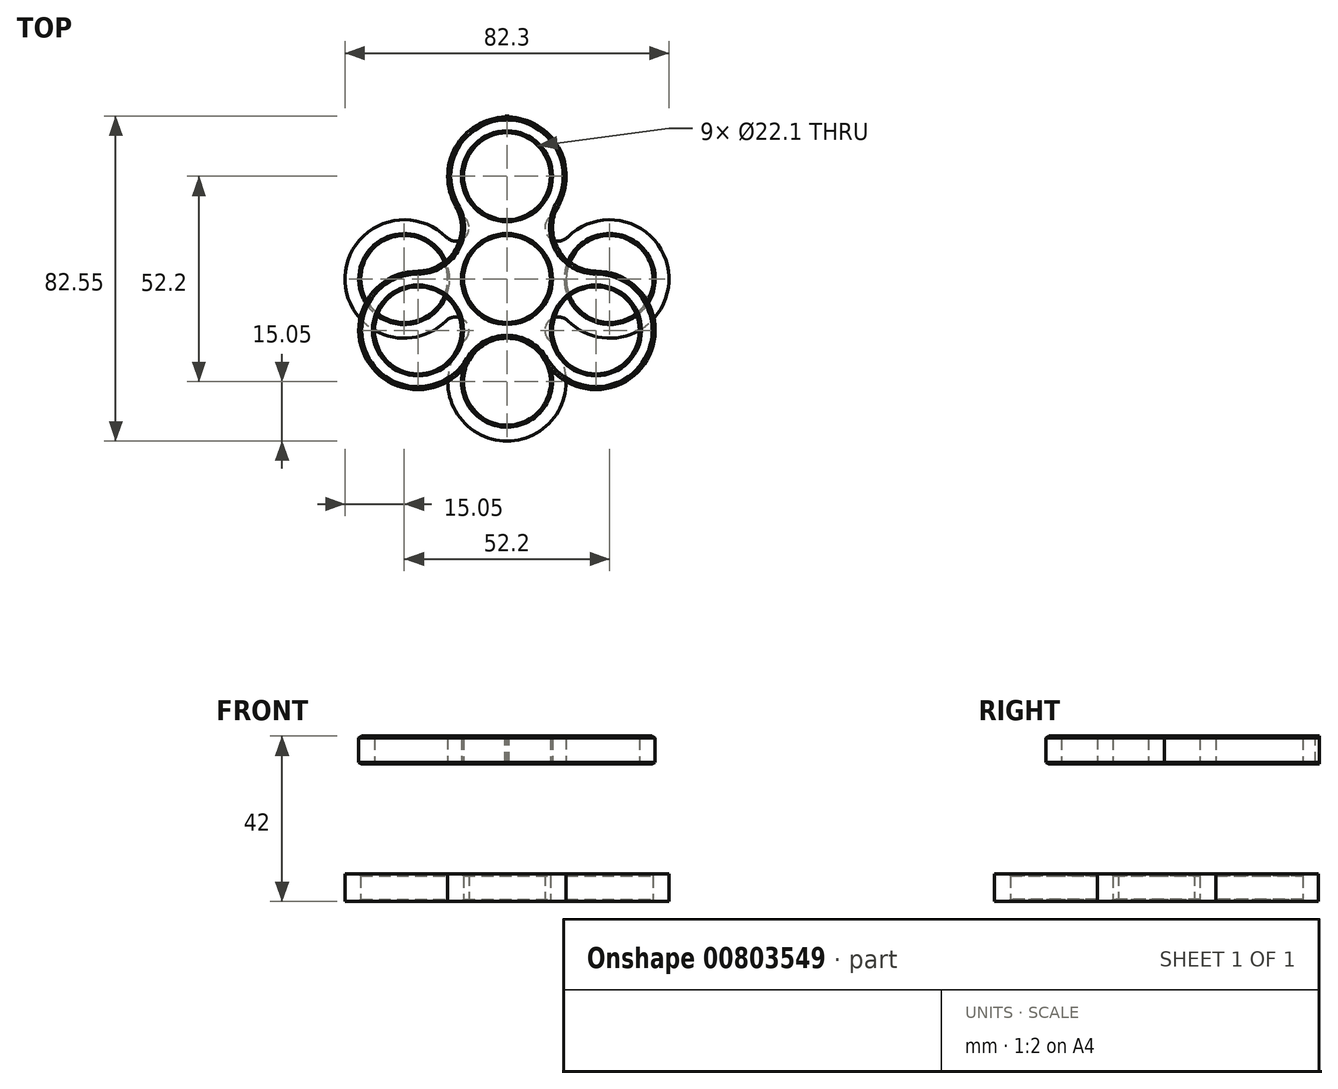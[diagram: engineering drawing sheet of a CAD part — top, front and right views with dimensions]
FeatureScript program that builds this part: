
annotation { "Feature Type Name" : "Feature", "Feature Type Description" : "" }
export const myFeature = defineFeature(function(context is Context, id is Id, definition is map)
    precondition{}
    {
        {
            var Q0;
            Q0=qCreatedBy(makeId("Top.planeOp"),FACE);
            var sketch = newSketch(context, id + "F0", { "sketchPlane" : qUnion([Q0])});
            skCircle(sketch, "E0", {"center": v(0, 0) * mm, "radius": 11.05 * mm});
            skCircle(sketch, "E1", {"center": v(0, 26.1) * mm, "radius": 11.05 * mm});
            skCircle(sketch, "E2", {"center": v(22.6, -13.05) * mm, "radius": 11.05 * mm});
            skCircle(sketch, "E3", {"center": v(-22.6, -13.05) * mm, "radius": 11.05 * mm});
            skLineSegment(sketch, "E4", {"start": v(0, 26.1) * mm, "end": v(-22.6, -13.05) * mm, "construction": true});
            skLineSegment(sketch, "E5", {"start": v(-22.6, -13.05) * mm, "end": v(22.6, -13.05) * mm, "construction": true});
            skLineSegment(sketch, "E6", {"start": v(22.6, -13.05) * mm, "end": v(0, 26.1) * mm, "construction": true});
            skLineSegment(sketch, "E7", {"start": v(11.3, 6.52) * mm, "end": v(-22.6, -13.05) * mm, "construction": true});
            skArc(sketch, "E8", {"start": v(13.03, 18.58) * mm, "mid": v(0, 41.15) * mm, "end": v(-13.03, 18.58) * mm});
            skLineSegment(sketch, "E9", {"start": v(-13.03, 7.52) * mm, "end": v(-13.03, 7.52) * mm});
            skArc(sketch, "E10", {"start": v(-22.6, 2) * mm, "mid": v(-35.64, -20.57) * mm, "end": v(-9.57, -20.58) * mm});
            skArc(sketch, "E11", {"start": v(9.57, -20.57) * mm, "mid": v(35.64, -20.57) * mm, "end": v(22.6, 2) * mm});
            skLineSegment(sketch, "E12.trimOffspring", {"start": v(13.03, 7.52) * mm, "end": v(13.03, 7.52) * mm});
            skLineSegment(sketch, "E13.trimOffspring", {"start": v(0, -15.05) * mm, "end": v(0, -15.05) * mm});
            skPoint(sketch, "E14.visualSharp", {"position": v(7.5, 13.05) * mm});
            skArc(sketch, "E14.filletArc", {"start": v(13.03, 18.58) * mm, "mid": v(11.55, 13.05) * mm, "end": v(13.03, 7.52) * mm});
            skPoint(sketch, "E15.visualSharp", {"position": v(15.05, -0.03) * mm});
            skArc(sketch, "E15.filletArc", {"start": v(13.03, 7.52) * mm, "mid": v(17.08, 3.48) * mm, "end": v(22.6, 2) * mm});
            skPoint(sketch, "E16.visualSharp", {"position": v(7.55, -13.02) * mm});
            skArc(sketch, "E16.filletArc", {"start": v(9.57, -20.57) * mm, "mid": v(5.52, -16.53) * mm, "end": v(0, -15.05) * mm});
            skPoint(sketch, "E17.visualSharp", {"position": v(-7.55, -13.02) * mm});
            skArc(sketch, "E17.filletArc", {"start": v(0, -15.05) * mm, "mid": v(-5.53, -16.53) * mm, "end": v(-9.57, -20.57) * mm});
            skPoint(sketch, "E18.visualSharp", {"position": v(-15.05, -0.03) * mm});
            skArc(sketch, "E18.filletArc", {"start": v(-22.6, 2) * mm, "mid": v(-17.08, 3.48) * mm, "end": v(-13.03, 7.52) * mm});
            skPoint(sketch, "E19.visualSharp", {"position": v(-7.5, 13.05) * mm});
            skArc(sketch, "E19.filletArc", {"start": v(-13.03, 7.52) * mm, "mid": v(-11.55, 13.05) * mm, "end": v(-13.03, 18.58) * mm});
            skCircle(sketch, "E20", {"center": v(0, 0) * mm, "radius": 41.15 * mm, "construction": true});
            skSolve(sketch);
        }
        {
            var Q0;
            Q0=makeQuery(id+"F0.imprint","IMPRINT",FACE,{"disambiguationData":[TD([[makeQuery(id+"F0.imprint","IMPRINT",EDGE,{"derivedFrom":sQuery(id+"F0.wireOp",EDGE,"E0")}),-1.0]])]});
            extrude(context, id + "F1", {"entities" : qUnion([Q0]), "depth" : 7 * mm, "offsetDistance" : 25 * mm});
        }
        {
            var Q0;
            Q0=makeQuery(id+"F1.opExtrude","SWEPT_FACE",FACE,{"disambiguationData":[OSD([sQuery(id+"F0.wireOp",EDGE,"E3")])]});
            var Q1;
            Q1=makeQuery(id+"F1.opExtrude","SWEPT_FACE",FACE,{"disambiguationData":[OSD([sQuery(id+"F0.wireOp",EDGE,"E0")])]});
            var Q2;
            Q2=makeQuery(id+"F1.opExtrude","SWEPT_FACE",FACE,{"disambiguationData":[OSD([sQuery(id+"F0.wireOp",EDGE,"E1")])]});
            var Q3;
            Q3=makeQuery(id+"F1.opExtrude","SWEPT_FACE",FACE,{"disambiguationData":[OSD([sQuery(id+"F0.wireOp",EDGE,"E2")])]});
            chamfer(context, id + "F2", {"entities" : qUnion([Q0, Q1, Q2, Q3]), "width" : .5 * mm, "tangentPropagation" : true});
        }
        {
            var Q0;
            Q0=makeQuery(id+"F2.opChamfer","SPLIT",FACE,{"disambiguationData":[OD(1.0)],"derivedFrom":makeQuery(id+"F1.opExtrude","CAP_FACE",FACE,{"disambiguationData":[OSD([sQuery(id+"F0.wireOp",EDGE,"E0"),sQuery(id+"F0.wireOp",EDGE,"E1"),sQuery(id+"F0.wireOp",EDGE,"E2"),sQuery(id+"F0.wireOp",EDGE,"E3"),sQuery(id+"F0.wireOp",EDGE,"E8"),sQuery(id+"F0.wireOp",EDGE,"E10"),sQuery(id+"F0.wireOp",EDGE,"E11"),sQuery(id+"F0.wireOp",EDGE,"E14.filletArc"),sQuery(id+"F0.wireOp",EDGE,"E15.filletArc"),sQuery(id+"F0.wireOp",EDGE,"E16.filletArc"),sQuery(id+"F0.wireOp",EDGE,"E17.filletArc"),sQuery(id+"F0.wireOp",EDGE,"E18.filletArc"),sQuery(id+"F0.wireOp",EDGE,"E19.filletArc")])],"isStart":true})});
            cPlane(context, id + "F3", {"entities" : qUnion([Q0]), "cplaneType" : CPlaneType.OFFSET, "offset" : 35 * mm, "width" : 150 * mm, "height" : 150 * mm});
        }
        {
            var Q0;
            Q0=qCreatedBy(id+"F3.planeOp",FACE);
            var sketch = newSketch(context, id + "F4", { "sketchPlane" : qUnion([Q0])});
            skCircle(sketch, "E21", {"center": v(0, 0) * mm, "radius": 11.05 * mm});
            skCircle(sketch, "E22", {"center": v(0, 26.1) * mm, "radius": 11.05 * mm});
            skCircle(sketch, "E23", {"center": v(26.1, 0) * mm, "radius": 11.05 * mm});
            skCircle(sketch, "E24", {"center": v(0, -26.1) * mm, "radius": 11.05 * mm});
            skCircle(sketch, "E25", {"center": v(-26.1, 0) * mm, "radius": 11.05 * mm});
            skLineSegment(sketch, "E26", {"start": v(0, 26.1) * mm, "end": v(0, 0) * mm, "construction": true});
            skLineSegment(sketch, "E27", {"start": v(26.1, 0) * mm, "end": v(0, 0) * mm, "construction": true});
            skLineSegment(sketch, "E28", {"start": v(0, -26.1) * mm, "end": v(0, 0) * mm, "construction": true});
            skLineSegment(sketch, "E29", {"start": v(-26.1, 0) * mm, "end": v(0, 0) * mm, "construction": true});
            skArc(sketch, "E30", {"start": v(10.64, 15.46) * mm, "mid": v(0, 41.15) * mm, "end": v(-10.64, 15.46) * mm});
            skArc(sketch, "E31", {"start": v(15.46, -10.64) * mm, "mid": v(41.15, 0) * mm, "end": v(15.46, 10.64) * mm});
            skArc(sketch, "E32", {"start": v(-7.5, 13.05) * mm, "mid": v(-10.64, 10.64) * mm, "end": v(-13.05, 7.5) * mm, "construction": true});
            skArc(sketch, "E33", {"start": v(-10.64, -15.46) * mm, "mid": v(0, -41.15) * mm, "end": v(10.64, -15.46) * mm});
            skArc(sketch, "E34", {"start": v(-15.46, 10.64) * mm, "mid": v(-41.15, 0) * mm, "end": v(-15.46, -10.64) * mm});
            skArc(sketch, "E35.trimOffspring", {"start": v(-13.05, -7.5) * mm, "mid": v(-10.64, -10.64) * mm, "end": v(-7.5, -13.05) * mm, "construction": true});
            skArc(sketch, "E36.trimOffspring", {"start": v(7.5, -13.05) * mm, "mid": v(10.64, -10.64) * mm, "end": v(13.05, -7.5) * mm, "construction": true});
            skArc(sketch, "E37.trimOffspring", {"start": v(13.05, 7.5) * mm, "mid": v(10.64, 10.64) * mm, "end": v(7.5, 13.05) * mm, "construction": true});
            skArc(sketch, "E38", {"start": v(10.64, 15.46) * mm, "mid": v(10.64, 10.64) * mm, "end": v(15.46, 10.64) * mm});
            skArc(sketch, "E39", {"start": v(15.46, -10.64) * mm, "mid": v(10.64, -10.64) * mm, "end": v(10.64, -15.46) * mm});
            skArc(sketch, "E40", {"start": v(-10.64, -15.46) * mm, "mid": v(-10.64, -10.64) * mm, "end": v(-15.46, -10.64) * mm});
            skArc(sketch, "E41", {"start": v(-15.46, 10.64) * mm, "mid": v(-10.64, 10.64) * mm, "end": v(-10.64, 15.46) * mm});
            skSolve(sketch);
        }
        {
            var Q0;
            Q0=makeQuery(id+"F4.imprint","IMPRINT",FACE,{"disambiguationData":[TD([[makeQuery(id+"F4.imprint","IMPRINT",EDGE,{"derivedFrom":sQuery(id+"F4.wireOp",EDGE,"E21")}),-1.0]])]});
            extrude(context, id + "F5", {"entities" : qUnion([Q0]), "oppositeDirection" : true, "depth" : 7 * mm, "offsetDistance" : 25 * mm});
        }
        {
            var Q0;
            Q0=makeQuery(id+"F5.opExtrude","SWEPT_FACE",FACE,{"disambiguationData":[OSD([sQuery(id+"F4.wireOp",EDGE,"E25")])]});
            var Q1;
            Q1=makeQuery(id+"F5.opExtrude","SWEPT_FACE",FACE,{"disambiguationData":[OSD([sQuery(id+"F4.wireOp",EDGE,"E21")])]});
            var Q2;
            Q2=makeQuery(id+"F5.opExtrude","SWEPT_FACE",FACE,{"disambiguationData":[OSD([sQuery(id+"F4.wireOp",EDGE,"E24")])]});
            var Q3;
            Q3=makeQuery(id+"F5.opExtrude","SWEPT_FACE",FACE,{"disambiguationData":[OSD([sQuery(id+"F4.wireOp",EDGE,"E23")])]});
            var Q4;
            Q4=makeQuery(id+"F5.opExtrude","SWEPT_FACE",FACE,{"disambiguationData":[OSD([sQuery(id+"F4.wireOp",EDGE,"E22")])]});
            chamfer(context, id + "F6", {"entities" : qUnion([Q0, Q1, Q2, Q3, Q4]), "width" : .5 * mm, "tangentPropagation" : true});
        }
        {
            var Q0;
            Q0=makeQuery(id+"F1.opExtrude","CAP_FACE",FACE,{"disambiguationData":[OSD([sQuery(id+"F0.wireOp",EDGE,"E0"),sQuery(id+"F0.wireOp",EDGE,"E1"),sQuery(id+"F0.wireOp",EDGE,"E2"),sQuery(id+"F0.wireOp",EDGE,"E3"),sQuery(id+"F0.wireOp",EDGE,"E8"),sQuery(id+"F0.wireOp",EDGE,"E10"),sQuery(id+"F0.wireOp",EDGE,"E11"),sQuery(id+"F0.wireOp",EDGE,"E14.filletArc"),sQuery(id+"F0.wireOp",EDGE,"E15.filletArc"),sQuery(id+"F0.wireOp",EDGE,"E16.filletArc"),sQuery(id+"F0.wireOp",EDGE,"E17.filletArc"),sQuery(id+"F0.wireOp",EDGE,"E18.filletArc"),sQuery(id+"F0.wireOp",EDGE,"E19.filletArc")])],"isStart":false});
            var sketch = newSketch(context, id + "F7", { "sketchPlane" : qUnion([Q0])});
            skLineSegment(sketch, "E42", {"start": v(0, 40.4) * mm, "end": v(0.52, 41.4) * mm});
            skPoint(sketch, "E42.startSnap0", {"position": v(0, 41.15) * mm});
            skLineSegment(sketch, "E43", {"start": v(0.52, 41.4) * mm, "end": v(-0.52, 41.4) * mm});
            skLineSegment(sketch, "E44", {"start": v(-0.52, 41.4) * mm, "end": v(0, 40.4) * mm});
            skPoint(sketch, "E45", {"position": v(-3.48, 40.74) * mm});
            skPoint(sketch, "E46", {"position": v(-6.76, 39.54) * mm});
            skLineSegment(sketch, "E47", {"start": v(0, 41.15) * mm, "end": v(-3.48, 40.74) * mm, "construction": true});
            skLineSegment(sketch, "E48", {"start": v(-3.48, 40.74) * mm, "end": v(-6.76, 39.54) * mm, "construction": true});
            skLineSegment(sketch, "E49", {"start": v(-6.76, 39.54) * mm, "end": v(-9.69, 37.62) * mm, "construction": true});
            skLineSegment(sketch, "E50", {"start": v(-9.69, 37.62) * mm, "end": v(-12.09, 35.07) * mm, "construction": true});
            skLineSegment(sketch, "E51", {"start": v(-12.09, 35.07) * mm, "end": v(-13.83, 32.04) * mm, "construction": true});
            skLineSegment(sketch, "E52", {"start": v(-13.83, 32.04) * mm, "end": v(-14.83, 28.68) * mm, "construction": true});
            skLineSegment(sketch, "E53", {"start": v(-14.83, 28.68) * mm, "end": v(-15.02, 25.19) * mm, "construction": true});
            skLineSegment(sketch, "E54", {"start": v(-15.02, 25.19) * mm, "end": v(-14.4, 21.74) * mm, "construction": true});
            skLineSegment(sketch, "E55", {"start": v(-14.4, 21.74) * mm, "end": v(-13, 18.53) * mm, "construction": true});
            skLineSegment(sketch, "E56", {"start": v(-13, 18.53) * mm, "end": v(-11.78, 15.26) * mm, "construction": true});
            skLineSegment(sketch, "E57", {"start": v(-11.78, 15.26) * mm, "end": v(-11.63, 11.76) * mm, "construction": true});
            skSolve(sketch);
        }
        {
            var Q0;
            {var subQ2=sQuery(id+"F0.wireOp",EDGE,"E8");Q0=makeQuery(id+"F9.boolean.opBoolean","SPLIT",EDGE,{"disambiguationData":[TD([makeQuery(id+"F9.opExtrude","SWEPT_FACE",FACE,{"disambiguationData":[OSD([sQuery(id+"F7.wireOp",EDGE,"E44")])]})])],"derivedFrom":makeQuery(id+"F1.opExtrude","CAP_EDGE",EDGE,{"disambiguationData":[OSD([subQ2])],"isStart":false})});}
            var Q1;
            {var subQ2=sQuery(id+"F0.wireOp",EDGE,"E8");Q1=makeQuery(id+"F9.boolean.opBoolean","SPLIT",EDGE,{"disambiguationData":[TD([makeQuery(id+"F9.opExtrude","SWEPT_FACE",FACE,{"disambiguationData":[OSD([sQuery(id+"F7.wireOp",EDGE,"E44")])]})])],"derivedFrom":makeQuery(id+"F1.opExtrude","CAP_EDGE",EDGE,{"disambiguationData":[OSD([subQ2])],"isStart":true})});}
            chamfer(context, id + "F8", {"entities" : qUnion([Q0, Q1]), "chamferType" : ChamferType.OFFSET_ANGLE, "width" : .75 * mm, "oppositeDirection" : false, "angle" : 27.5 * degree, "tangentPropagation" : true});
        }
        {
            var Q0;
            {var subQ0=sQuery(id+"F7.wireOp",EDGE,"E44");var subQ1=sQuery(id+"F7.wireOp",EDGE,"E42");var subQ2=makeQuery(id+"F7.imprint","INTERSECT",VERTEX,{"derivedFrom":[subQ1,subQ0]});Q0=makeQuery(id+"F7.imprint","IMPRINT",FACE,{"disambiguationData":[TD([[makeQuery(id+"F7.imprint","IMPRINT",EDGE,{"disambiguationData":[TD([[subQ2,-1.0]])],"derivedFrom":subQ1}),1.0]])]});}
            var Q1;
            {var subQ0=sQuery(id+"F7.wireOp",EDGE,"E43");Q1=makeQuery(id+"F7.imprint","IMPRINT",FACE,{"disambiguationData":[TD([[makeQuery(id+"F7.imprint","IMPRINT",EDGE,{"derivedFrom":subQ0}),1.0]])]});}
            var Q2;
            Q2=makeQuery(id+"F1.opExtrude","CAP_FACE",FACE,{"disambiguationData":[OSD([sQuery(id+"F0.wireOp",EDGE,"E0"),sQuery(id+"F0.wireOp",EDGE,"E1"),sQuery(id+"F0.wireOp",EDGE,"E2"),sQuery(id+"F0.wireOp",EDGE,"E3"),sQuery(id+"F0.wireOp",EDGE,"E8"),sQuery(id+"F0.wireOp",EDGE,"E10"),sQuery(id+"F0.wireOp",EDGE,"E11"),sQuery(id+"F0.wireOp",EDGE,"E14.filletArc"),sQuery(id+"F0.wireOp",EDGE,"E15.filletArc"),sQuery(id+"F0.wireOp",EDGE,"E16.filletArc"),sQuery(id+"F0.wireOp",EDGE,"E17.filletArc"),sQuery(id+"F0.wireOp",EDGE,"E18.filletArc"),sQuery(id+"F0.wireOp",EDGE,"E19.filletArc")])],"isStart":true});
            extrude(context, id + "F9", {"entities" : qUnion([Q0, Q1]), "endBound" : BoundingType.UP_TO_SURFACE, "oppositeDirection" : true, "depth" : 25 * mm, "endBoundEntityFace" : qUnion([Q2]), "offsetDistance" : 25 * mm});
        }
    });
